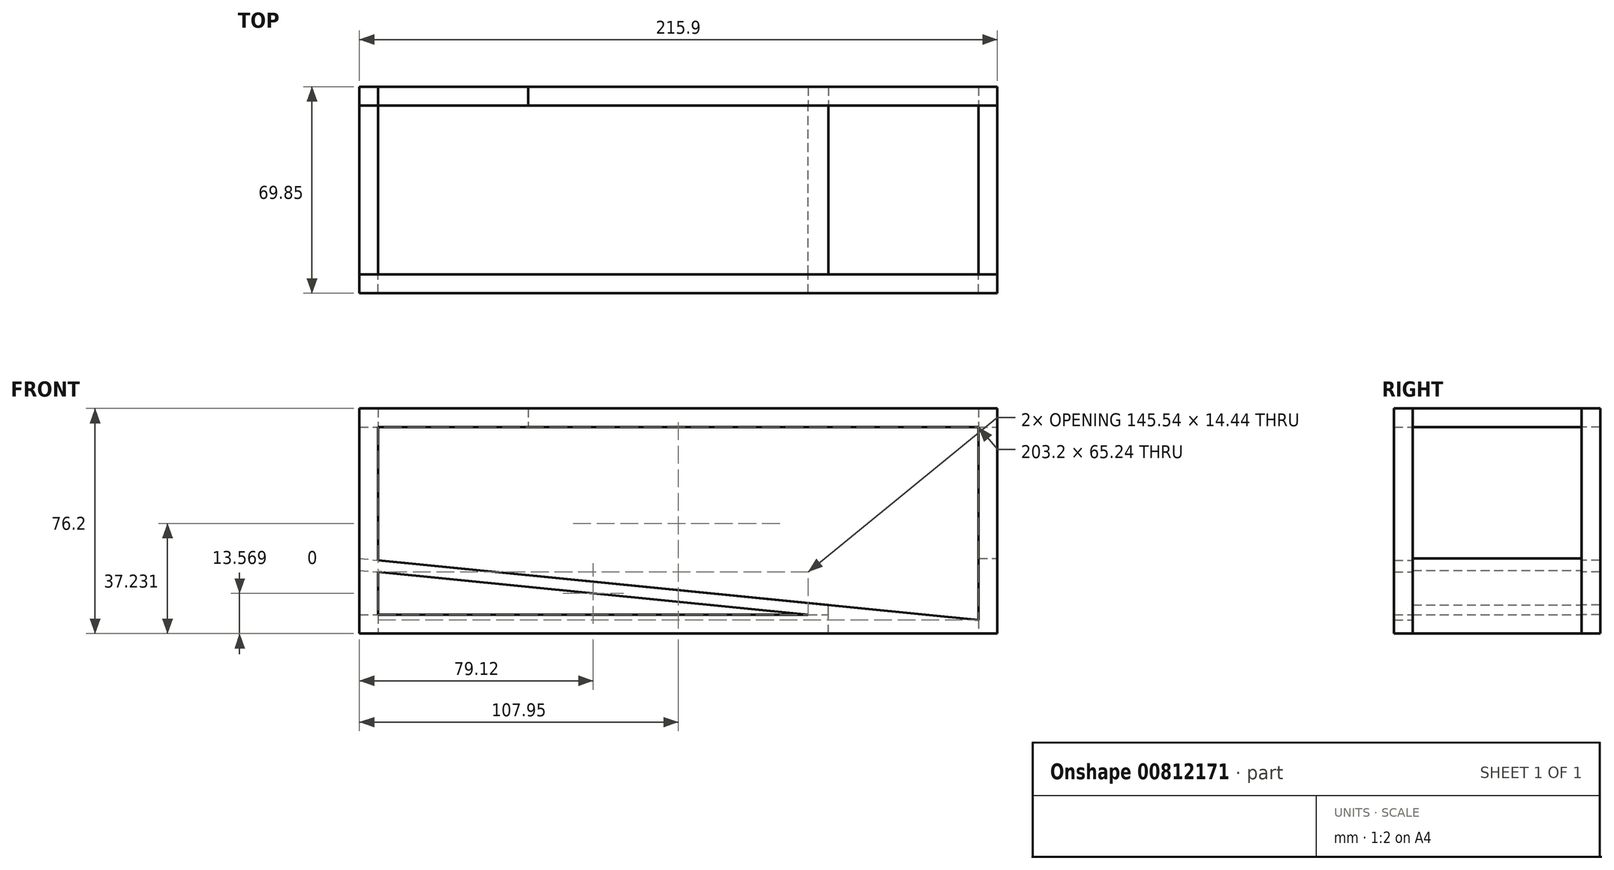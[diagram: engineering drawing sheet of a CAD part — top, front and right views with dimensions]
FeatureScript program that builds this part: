
annotation { "Feature Type Name" : "Feature", "Feature Type Description" : "" }
export const myFeature = defineFeature(function(context is Context, id is Id, definition is map)
    precondition{}
    {
        {
            var Q0;
            Q0=qCreatedBy(makeId("Front.planeOp"),FACE);
            var sketch = newSketch(context, id + "F0", { "sketchPlane" : qUnion([Q0])});
            skLineSegment(sketch, "E0.bottom", {"start": v(0, 76.2) * mm, "end": v(215.9, 76.2) * mm});
            skLineSegment(sketch, "E0.top", {"start": v(0, 0) * mm, "end": v(215.9, 0) * mm});
            skLineSegment(sketch, "E0.left", {"start": v(0, 76.2) * mm, "end": v(0, 0) * mm});
            skLineSegment(sketch, "E0.right", {"start": v(215.9, 76.2) * mm, "end": v(215.9, 0) * mm});
            skLineSegment(sketch, "E1.0", {"start": v(0, 69.85) * mm, "end": v(215.9, 69.85) * mm});
            skLineSegment(sketch, "E1.1", {"start": v(6.35, 76.2) * mm, "end": v(6.35, 0) * mm});
            skLineSegment(sketch, "E1.2", {"start": v(0, 6.35) * mm, "end": v(215.9, 6.35) * mm});
            skLineSegment(sketch, "E1.3", {"start": v(209.55, 76.2) * mm, "end": v(209.55, 0) * mm});
            skLineSegment(sketch, "E2", {"start": v(0, 25.4) * mm, "end": v(215.9, 3.98) * mm});
            skLineSegment(sketch, "E3.0", {"start": v(0, 21.42) * mm, "end": v(215.9, 0) * mm});
            skLineSegment(sketch, "E4", {"start": v(209.55, 25.4) * mm, "end": v(215.9, 25.4) * mm});
            skLineSegment(sketch, "E5.0", {"start": v(0, 29.38) * mm, "end": v(215.9, 7.96) * mm});
            skLineSegment(sketch, "E6", {"start": v(158.75, 0) * mm, "end": v(158.75, 13.63) * mm});
            skLineSegment(sketch, "E7", {"start": v(57.15, 76.2) * mm, "end": v(57.15, 69.85) * mm});
            skSolve(sketch);
        }
        {
            var Q0;
            {var subQ1=sQuery(id+"F0.wireOp",EDGE,"E1.1");var subQ5=sQuery(id+"F0.wireOp",EDGE,"E2");var subQ6=makeQuery(id+"F0.imprint","INTERSECT",VERTEX,{"derivedFrom":[subQ1,subQ5]});Q0=makeQuery(id+"F0.imprint","IMPRINT",FACE,{"disambiguationData":[TD([[makeQuery(id+"F0.imprint","IMPRINT",EDGE,{"disambiguationData":[TD([[subQ6,-1.0]])],"derivedFrom":subQ1}),1.0]])]});}
            var Q1;
            {var subQ0=sQuery(id+"F0.wireOp",EDGE,"E2");var subQ1=sQuery(id+"F0.wireOp",EDGE,"E0.left");var subQ2=makeQuery(id+"F0.imprint","INTERSECT",VERTEX,{"derivedFrom":[subQ1,subQ0]});Q1=makeQuery(id+"F0.imprint","IMPRINT",FACE,{"disambiguationData":[TD([[makeQuery(id+"F0.imprint","IMPRINT",EDGE,{"disambiguationData":[TD([[subQ2,-1.0]])],"derivedFrom":subQ1}),1.0]])]});}
            var Q2;
            {var subQ0=sQuery(id+"F0.wireOp",EDGE,"E2");var subQ1=sQuery(id+"F0.wireOp",EDGE,"E0.left");var subQ2=makeQuery(id+"F0.imprint","INTERSECT",VERTEX,{"derivedFrom":[subQ1,subQ0]});Q2=makeQuery(id+"F0.imprint","IMPRINT",FACE,{"disambiguationData":[TD([[makeQuery(id+"F0.imprint","IMPRINT",EDGE,{"disambiguationData":[TD([[subQ2,1.0]])],"derivedFrom":subQ1}),1.0]])]});}
            var Q3;
            {var subQ0=sQuery(id+"F0.wireOp",EDGE,"E1.0");var subQ1=sQuery(id+"F0.wireOp",EDGE,"E0.left");var subQ2=makeQuery(id+"F0.imprint","INTERSECT",VERTEX,{"derivedFrom":[subQ1,subQ0]});Q3=makeQuery(id+"F0.imprint","IMPRINT",FACE,{"disambiguationData":[TD([[makeQuery(id+"F0.imprint","IMPRINT",EDGE,{"disambiguationData":[TD([[subQ2,-1.0]])],"derivedFrom":subQ1}),1.0]])]});}
            var Q4;
            {var subQ0=sQuery(id+"F0.wireOp",EDGE,"E0.left");var subQ1=sQuery(id+"F0.wireOp",EDGE,"E0.bottom");var subQ2=makeQuery(id+"F0.imprint","INTERSECT",VERTEX,{"derivedFrom":[subQ1,subQ0]});Q4=makeQuery(id+"F0.imprint","IMPRINT",FACE,{"disambiguationData":[TD([[makeQuery(id+"F0.imprint","IMPRINT",EDGE,{"disambiguationData":[TD([[subQ2,-1.0]])],"derivedFrom":subQ1}),-1.0]])]});}
            var Q5;
            {var subQ0=sQuery(id+"F0.wireOp",EDGE,"E0.right");var subQ1=sQuery(id+"F0.wireOp",EDGE,"E0.bottom");var subQ2=makeQuery(id+"F0.imprint","INTERSECT",VERTEX,{"derivedFrom":[subQ1,subQ0]});Q5=makeQuery(id+"F0.imprint","IMPRINT",FACE,{"disambiguationData":[TD([[makeQuery(id+"F0.imprint","IMPRINT",EDGE,{"disambiguationData":[TD([[subQ2,1.0]])],"derivedFrom":subQ1}),-1.0]])]});}
            var Q6;
            {var subQ3=sQuery(id+"F0.wireOp",EDGE,"E4");Q6=makeQuery(id+"F0.imprint","IMPRINT",FACE,{"disambiguationData":[TD([[makeQuery(id+"F0.imprint","IMPRINT",EDGE,{"derivedFrom":subQ3}),1.0]])]});}
            var Q7;
            {var subQ0=sQuery(id+"F0.wireOp",EDGE,"E4");Q7=makeQuery(id+"F0.imprint","IMPRINT",FACE,{"disambiguationData":[TD([[makeQuery(id+"F0.imprint","IMPRINT",EDGE,{"derivedFrom":subQ0}),-1.0]])]});}
            var Q8;
            {var subQ0=sQuery(id+"F0.wireOp",EDGE,"E1.2");var subQ1=sQuery(id+"F0.wireOp",EDGE,"E0.right");var subQ2=makeQuery(id+"F0.imprint","INTERSECT",VERTEX,{"derivedFrom":[subQ1,subQ0]});Q8=makeQuery(id+"F0.imprint","IMPRINT",FACE,{"disambiguationData":[TD([[makeQuery(id+"F0.imprint","IMPRINT",EDGE,{"disambiguationData":[TD([[subQ2,1.0]])],"derivedFrom":subQ1}),-1.0]])]});}
            var Q9;
            {var subQ0=sQuery(id+"F0.wireOp",EDGE,"E1.2");var subQ1=sQuery(id+"F0.wireOp",EDGE,"E0.right");var subQ2=makeQuery(id+"F0.imprint","INTERSECT",VERTEX,{"derivedFrom":[subQ1,subQ0]});Q9=makeQuery(id+"F0.imprint","IMPRINT",FACE,{"disambiguationData":[TD([[makeQuery(id+"F0.imprint","IMPRINT",EDGE,{"disambiguationData":[TD([[subQ2,-1.0]])],"derivedFrom":subQ1}),-1.0]])]});}
            var Q10;
            {var subQ1=sQuery(id+"F0.wireOp",EDGE,"E0.top");var subQ3=sQuery(id+"F0.wireOp",EDGE,"E1.3");var subQ4=makeQuery(id+"F0.imprint","INTERSECT",VERTEX,{"derivedFrom":[subQ1,subQ3]});Q10=makeQuery(id+"F0.imprint","IMPRINT",FACE,{"disambiguationData":[TD([[makeQuery(id+"F0.imprint","IMPRINT",EDGE,{"disambiguationData":[TD([[subQ4,1.0]])],"derivedFrom":subQ3}),1.0]])]});}
            var Q11;
            {var subQ3=sQuery(id+"F0.wireOp",EDGE,"E2");var subQ5=sQuery(id+"F0.wireOp",EDGE,"E1.3");var subQ6=makeQuery(id+"F0.imprint","INTERSECT",VERTEX,{"derivedFrom":[subQ5,subQ3]});Q11=makeQuery(id+"F0.imprint","IMPRINT",FACE,{"disambiguationData":[TD([[makeQuery(id+"F0.imprint","IMPRINT",EDGE,{"disambiguationData":[TD([[subQ6,-1.0]])],"derivedFrom":subQ5}),1.0]])]});}
            var Q12;
            {var subQ0=sQuery(id+"F0.wireOp",EDGE,"E1.2");var subQ1=sQuery(id+"F0.wireOp",EDGE,"E0.left");var subQ2=makeQuery(id+"F0.imprint","INTERSECT",VERTEX,{"derivedFrom":[subQ1,subQ0]});Q12=makeQuery(id+"F0.imprint","IMPRINT",FACE,{"disambiguationData":[TD([[makeQuery(id+"F0.imprint","IMPRINT",EDGE,{"disambiguationData":[TD([[subQ2,1.0]])],"derivedFrom":subQ1}),1.0]])]});}
            var Q13;
            {var subQ0=sQuery(id+"F0.wireOp",EDGE,"E0.left");var subQ1=sQuery(id+"F0.wireOp",EDGE,"E0.top");var subQ2=makeQuery(id+"F0.imprint","INTERSECT",VERTEX,{"derivedFrom":[subQ1,subQ0]});Q13=makeQuery(id+"F0.imprint","IMPRINT",FACE,{"disambiguationData":[TD([[makeQuery(id+"F0.imprint","IMPRINT",EDGE,{"disambiguationData":[TD([[subQ2,-1.0]])],"derivedFrom":subQ1}),1.0]])]});}
            var Q14;
            {var subQ3=sQuery(id+"F0.wireOp",EDGE,"E7");Q14=makeQuery(id+"F0.imprint","IMPRINT",FACE,{"disambiguationData":[TD([[makeQuery(id+"F0.imprint","IMPRINT",EDGE,{"derivedFrom":subQ3}),1.0]])]});}
            var Q15;
            {var subQ0=sQuery(id+"F0.wireOp",EDGE,"E3.0");var subQ1=sQuery(id+"F0.wireOp",EDGE,"E1.2");var subQ2=makeQuery(id+"F0.imprint","INTERSECT",VERTEX,{"derivedFrom":[subQ1,subQ0]});Q15=makeQuery(id+"F0.imprint","IMPRINT",FACE,{"disambiguationData":[TD([[makeQuery(id+"F0.imprint","IMPRINT",EDGE,{"disambiguationData":[TD([[subQ2,-1.0]])],"derivedFrom":subQ1}),-1.0]])]});}
            var Q16;
            {var subQ1=sQuery(id+"F0.wireOp",EDGE,"E0.top");var subQ6=sQuery(id+"F0.wireOp",EDGE,"E1.1");var subQ9=makeQuery(id+"F0.imprint","INTERSECT",VERTEX,{"derivedFrom":[subQ1,subQ6]});Q16=makeQuery(id+"F0.imprint","IMPRINT",FACE,{"disambiguationData":[TD([[makeQuery(id+"F0.imprint","IMPRINT",EDGE,{"disambiguationData":[TD([[subQ9,-1.0]])],"derivedFrom":subQ1}),1.0]])]});}
            extrude(context, id + "F1", {"entities" : qUnion([Q0, Q1, Q2, Q3, Q4, Q5, Q6, Q7, Q8, Q9, Q10, Q11, Q12, Q13, Q14, Q15, Q16]), "oppositeDirection" : true, "depth" : 6.35 * mm, "offsetDistance" : 25.4 * mm});
        }
        {
            var Q0;
            {var subQ3=sQuery(id+"F0.wireOp",EDGE,"E2");var subQ5=sQuery(id+"F0.wireOp",EDGE,"E1.3");var subQ6=makeQuery(id+"F0.imprint","INTERSECT",VERTEX,{"derivedFrom":[subQ5,subQ3]});Q0=makeQuery(id+"F0.imprint","IMPRINT",FACE,{"disambiguationData":[TD([[makeQuery(id+"F0.imprint","IMPRINT",EDGE,{"disambiguationData":[TD([[subQ6,-1.0]])],"derivedFrom":subQ5}),1.0]])]});}
            var Q1;
            {var subQ1=sQuery(id+"F0.wireOp",EDGE,"E0.top");var subQ3=sQuery(id+"F0.wireOp",EDGE,"E1.3");var subQ4=makeQuery(id+"F0.imprint","INTERSECT",VERTEX,{"derivedFrom":[subQ1,subQ3]});Q1=makeQuery(id+"F0.imprint","IMPRINT",FACE,{"disambiguationData":[TD([[makeQuery(id+"F0.imprint","IMPRINT",EDGE,{"disambiguationData":[TD([[subQ4,1.0]])],"derivedFrom":subQ3}),1.0]])]});}
            var Q2;
            {var subQ0=sQuery(id+"F0.wireOp",EDGE,"E1.3");var subQ1=sQuery(id+"F0.wireOp",EDGE,"E0.top");var subQ2=makeQuery(id+"F0.imprint","INTERSECT",VERTEX,{"derivedFrom":[subQ1,subQ0]});Q2=makeQuery(id+"F0.imprint","IMPRINT",FACE,{"disambiguationData":[TD([[makeQuery(id+"F0.imprint","IMPRINT",EDGE,{"disambiguationData":[TD([[subQ2,1.0]])],"derivedFrom":subQ1}),1.0]])]});}
            var Q3;
            {var subQ3=sQuery(id+"F0.wireOp",EDGE,"E6");var subQ6=sQuery(id+"F0.wireOp",EDGE,"E1.2");var subQ9=makeQuery(id+"F0.imprint","INTERSECT",VERTEX,{"derivedFrom":[subQ6,subQ3]});Q3=makeQuery(id+"F0.imprint","IMPRINT",FACE,{"disambiguationData":[TD([[makeQuery(id+"F0.imprint","IMPRINT",EDGE,{"disambiguationData":[TD([[subQ9,-1.0]])],"derivedFrom":subQ6}),-1.0]])]});}
            var Q4;
            {var subQ0=sQuery(id+"F0.wireOp",EDGE,"E6");var subQ1=sQuery(id+"F0.wireOp",EDGE,"E1.2");var subQ2=makeQuery(id+"F0.imprint","INTERSECT",VERTEX,{"derivedFrom":[subQ1,subQ0]});Q4=makeQuery(id+"F0.imprint","IMPRINT",FACE,{"disambiguationData":[TD([[makeQuery(id+"F0.imprint","IMPRINT",EDGE,{"disambiguationData":[TD([[subQ2,-1.0]])],"derivedFrom":subQ1}),1.0]])]});}
            var Q5;
            {var subQ1=sQuery(id+"F0.wireOp",EDGE,"E1.1");var subQ5=sQuery(id+"F0.wireOp",EDGE,"E2");var subQ6=makeQuery(id+"F0.imprint","INTERSECT",VERTEX,{"derivedFrom":[subQ1,subQ5]});Q5=makeQuery(id+"F0.imprint","IMPRINT",FACE,{"disambiguationData":[TD([[makeQuery(id+"F0.imprint","IMPRINT",EDGE,{"disambiguationData":[TD([[subQ6,-1.0]])],"derivedFrom":subQ1}),1.0]])]});}
            var Q6;
            {var subQ0=sQuery(id+"F0.wireOp",EDGE,"E3.0");var subQ1=sQuery(id+"F0.wireOp",EDGE,"E1.2");var subQ2=makeQuery(id+"F0.imprint","INTERSECT",VERTEX,{"derivedFrom":[subQ1,subQ0]});Q6=makeQuery(id+"F0.imprint","IMPRINT",FACE,{"disambiguationData":[TD([[makeQuery(id+"F0.imprint","IMPRINT",EDGE,{"disambiguationData":[TD([[subQ2,-1.0]])],"derivedFrom":subQ1}),-1.0]])]});}
            var Q7;
            {var subQ1=sQuery(id+"F0.wireOp",EDGE,"E1.1");var subQ5=sQuery(id+"F0.wireOp",EDGE,"E0.top");var subQ6=makeQuery(id+"F0.imprint","INTERSECT",VERTEX,{"derivedFrom":[subQ5,subQ1]});Q7=makeQuery(id+"F0.imprint","IMPRINT",FACE,{"disambiguationData":[TD([[makeQuery(id+"F0.imprint","IMPRINT",EDGE,{"disambiguationData":[TD([[subQ6,-1.0]])],"derivedFrom":subQ5}),1.0]])]});}
            var Q8;
            {var subQ0=sQuery(id+"F0.wireOp",EDGE,"E4");Q8=makeQuery(id+"F0.imprint","IMPRINT",FACE,{"disambiguationData":[TD([[makeQuery(id+"F0.imprint","IMPRINT",EDGE,{"derivedFrom":subQ0}),-1.0]])]});}
            var Q9;
            {var subQ0=sQuery(id+"F0.wireOp",EDGE,"E1.2");var subQ1=sQuery(id+"F0.wireOp",EDGE,"E0.right");var subQ2=makeQuery(id+"F0.imprint","INTERSECT",VERTEX,{"derivedFrom":[subQ1,subQ0]});Q9=makeQuery(id+"F0.imprint","IMPRINT",FACE,{"disambiguationData":[TD([[makeQuery(id+"F0.imprint","IMPRINT",EDGE,{"disambiguationData":[TD([[subQ2,-1.0]])],"derivedFrom":subQ1}),-1.0]])]});}
            var Q10;
            {var subQ0=sQuery(id+"F0.wireOp",EDGE,"E1.2");var subQ1=sQuery(id+"F0.wireOp",EDGE,"E0.right");var subQ2=makeQuery(id+"F0.imprint","INTERSECT",VERTEX,{"derivedFrom":[subQ1,subQ0]});Q10=makeQuery(id+"F0.imprint","IMPRINT",FACE,{"disambiguationData":[TD([[makeQuery(id+"F0.imprint","IMPRINT",EDGE,{"disambiguationData":[TD([[subQ2,1.0]])],"derivedFrom":subQ1}),-1.0]])]});}
            var Q11;
            {var subQ3=sQuery(id+"F0.wireOp",EDGE,"E4");Q11=makeQuery(id+"F0.imprint","IMPRINT",FACE,{"disambiguationData":[TD([[makeQuery(id+"F0.imprint","IMPRINT",EDGE,{"derivedFrom":subQ3}),1.0]])]});}
            var Q12;
            {var subQ0=sQuery(id+"F0.wireOp",EDGE,"E0.right");var subQ1=sQuery(id+"F0.wireOp",EDGE,"E0.bottom");var subQ2=makeQuery(id+"F0.imprint","INTERSECT",VERTEX,{"derivedFrom":[subQ1,subQ0]});Q12=makeQuery(id+"F0.imprint","IMPRINT",FACE,{"disambiguationData":[TD([[makeQuery(id+"F0.imprint","IMPRINT",EDGE,{"disambiguationData":[TD([[subQ2,1.0]])],"derivedFrom":subQ1}),-1.0]])]});}
            var Q13;
            {var subQ3=sQuery(id+"F0.wireOp",EDGE,"E7");Q13=makeQuery(id+"F0.imprint","IMPRINT",FACE,{"disambiguationData":[TD([[makeQuery(id+"F0.imprint","IMPRINT",EDGE,{"derivedFrom":subQ3}),1.0]])]});}
            var Q14;
            {var subQ0=sQuery(id+"F0.wireOp",EDGE,"E0.left");var subQ1=sQuery(id+"F0.wireOp",EDGE,"E0.top");var subQ2=makeQuery(id+"F0.imprint","INTERSECT",VERTEX,{"derivedFrom":[subQ1,subQ0]});Q14=makeQuery(id+"F0.imprint","IMPRINT",FACE,{"disambiguationData":[TD([[makeQuery(id+"F0.imprint","IMPRINT",EDGE,{"disambiguationData":[TD([[subQ2,-1.0]])],"derivedFrom":subQ1}),1.0]])]});}
            var Q15;
            {var subQ0=sQuery(id+"F0.wireOp",EDGE,"E1.2");var subQ1=sQuery(id+"F0.wireOp",EDGE,"E0.left");var subQ2=makeQuery(id+"F0.imprint","INTERSECT",VERTEX,{"derivedFrom":[subQ1,subQ0]});Q15=makeQuery(id+"F0.imprint","IMPRINT",FACE,{"disambiguationData":[TD([[makeQuery(id+"F0.imprint","IMPRINT",EDGE,{"disambiguationData":[TD([[subQ2,1.0]])],"derivedFrom":subQ1}),1.0]])]});}
            var Q16;
            {var subQ0=sQuery(id+"F0.wireOp",EDGE,"E2");var subQ1=sQuery(id+"F0.wireOp",EDGE,"E0.left");var subQ2=makeQuery(id+"F0.imprint","INTERSECT",VERTEX,{"derivedFrom":[subQ1,subQ0]});Q16=makeQuery(id+"F0.imprint","IMPRINT",FACE,{"disambiguationData":[TD([[makeQuery(id+"F0.imprint","IMPRINT",EDGE,{"disambiguationData":[TD([[subQ2,-1.0]])],"derivedFrom":subQ1}),1.0]])]});}
            var Q17;
            {var subQ0=sQuery(id+"F0.wireOp",EDGE,"E2");var subQ1=sQuery(id+"F0.wireOp",EDGE,"E0.left");var subQ2=makeQuery(id+"F0.imprint","INTERSECT",VERTEX,{"derivedFrom":[subQ1,subQ0]});Q17=makeQuery(id+"F0.imprint","IMPRINT",FACE,{"disambiguationData":[TD([[makeQuery(id+"F0.imprint","IMPRINT",EDGE,{"disambiguationData":[TD([[subQ2,1.0]])],"derivedFrom":subQ1}),1.0]])]});}
            var Q18;
            {var subQ0=sQuery(id+"F0.wireOp",EDGE,"E1.0");var subQ1=sQuery(id+"F0.wireOp",EDGE,"E0.left");var subQ2=makeQuery(id+"F0.imprint","INTERSECT",VERTEX,{"derivedFrom":[subQ1,subQ0]});Q18=makeQuery(id+"F0.imprint","IMPRINT",FACE,{"disambiguationData":[TD([[makeQuery(id+"F0.imprint","IMPRINT",EDGE,{"disambiguationData":[TD([[subQ2,-1.0]])],"derivedFrom":subQ1}),1.0]])]});}
            var Q19;
            {var subQ0=sQuery(id+"F0.wireOp",EDGE,"E0.left");var subQ1=sQuery(id+"F0.wireOp",EDGE,"E0.bottom");var subQ2=makeQuery(id+"F0.imprint","INTERSECT",VERTEX,{"derivedFrom":[subQ1,subQ0]});Q19=makeQuery(id+"F0.imprint","IMPRINT",FACE,{"disambiguationData":[TD([[makeQuery(id+"F0.imprint","IMPRINT",EDGE,{"disambiguationData":[TD([[subQ2,-1.0]])],"derivedFrom":subQ1}),-1.0]])]});}
            var Q20;
            {var subQ3=sQuery(id+"F0.wireOp",EDGE,"E7");Q20=makeQuery(id+"F0.imprint","IMPRINT",FACE,{"disambiguationData":[TD([[makeQuery(id+"F0.imprint","IMPRINT",EDGE,{"derivedFrom":subQ3}),-1.0]])]});}
            extrude(context, id + "F2", {"entities" : qUnion([Q0, Q1, Q2, Q3, Q4, Q5, Q6, Q7, Q8, Q9, Q10, Q11, Q12, Q13, Q14, Q15, Q16, Q17, Q18, Q19, Q20]), "depth" : 63.5 * mm, "offsetDistance" : 25.4 * mm, "hasSecondDirection" : true, "secondDirectionOppositeDirection" : true, "secondDirectionDepth" : -57.15 * mm});
        }
        {
            var Q0;
            {var subQ0=sQuery(id+"F0.wireOp",EDGE,"E0.right");var subQ1=sQuery(id+"F0.wireOp",EDGE,"E0.bottom");var subQ2=makeQuery(id+"F0.imprint","INTERSECT",VERTEX,{"derivedFrom":[subQ1,subQ0]});Q0=makeQuery(id+"F0.imprint","IMPRINT",FACE,{"disambiguationData":[TD([[makeQuery(id+"F0.imprint","IMPRINT",EDGE,{"disambiguationData":[TD([[subQ2,1.0]])],"derivedFrom":subQ1}),-1.0]])]});}
            var Q1;
            {var subQ1=sQuery(id+"F0.wireOp",EDGE,"E0.top");var subQ3=sQuery(id+"F0.wireOp",EDGE,"E1.3");var subQ4=makeQuery(id+"F0.imprint","INTERSECT",VERTEX,{"derivedFrom":[subQ1,subQ3]});Q1=makeQuery(id+"F0.imprint","IMPRINT",FACE,{"disambiguationData":[TD([[makeQuery(id+"F0.imprint","IMPRINT",EDGE,{"disambiguationData":[TD([[subQ4,1.0]])],"derivedFrom":subQ3}),1.0]])]});}
            var Q2;
            {var subQ3=sQuery(id+"F0.wireOp",EDGE,"E2");var subQ5=sQuery(id+"F0.wireOp",EDGE,"E1.3");var subQ6=makeQuery(id+"F0.imprint","INTERSECT",VERTEX,{"derivedFrom":[subQ5,subQ3]});Q2=makeQuery(id+"F0.imprint","IMPRINT",FACE,{"disambiguationData":[TD([[makeQuery(id+"F0.imprint","IMPRINT",EDGE,{"disambiguationData":[TD([[subQ6,-1.0]])],"derivedFrom":subQ5}),1.0]])]});}
            var Q3;
            {var subQ0=sQuery(id+"F0.wireOp",EDGE,"E1.2");var subQ1=sQuery(id+"F0.wireOp",EDGE,"E0.right");var subQ2=makeQuery(id+"F0.imprint","INTERSECT",VERTEX,{"derivedFrom":[subQ1,subQ0]});Q3=makeQuery(id+"F0.imprint","IMPRINT",FACE,{"disambiguationData":[TD([[makeQuery(id+"F0.imprint","IMPRINT",EDGE,{"disambiguationData":[TD([[subQ2,-1.0]])],"derivedFrom":subQ1}),-1.0]])]});}
            var Q4;
            {var subQ0=sQuery(id+"F0.wireOp",EDGE,"E1.2");var subQ1=sQuery(id+"F0.wireOp",EDGE,"E0.right");var subQ2=makeQuery(id+"F0.imprint","INTERSECT",VERTEX,{"derivedFrom":[subQ1,subQ0]});Q4=makeQuery(id+"F0.imprint","IMPRINT",FACE,{"disambiguationData":[TD([[makeQuery(id+"F0.imprint","IMPRINT",EDGE,{"disambiguationData":[TD([[subQ2,1.0]])],"derivedFrom":subQ1}),-1.0]])]});}
            var Q5;
            {var subQ0=sQuery(id+"F0.wireOp",EDGE,"E4");Q5=makeQuery(id+"F0.imprint","IMPRINT",FACE,{"disambiguationData":[TD([[makeQuery(id+"F0.imprint","IMPRINT",EDGE,{"derivedFrom":subQ0}),-1.0]])]});}
            var Q6;
            {var subQ0=sQuery(id+"F0.wireOp",EDGE,"E0.left");var subQ1=sQuery(id+"F0.wireOp",EDGE,"E0.bottom");var subQ2=makeQuery(id+"F0.imprint","INTERSECT",VERTEX,{"derivedFrom":[subQ1,subQ0]});Q6=makeQuery(id+"F0.imprint","IMPRINT",FACE,{"disambiguationData":[TD([[makeQuery(id+"F0.imprint","IMPRINT",EDGE,{"disambiguationData":[TD([[subQ2,-1.0]])],"derivedFrom":subQ1}),-1.0]])]});}
            var Q7;
            {var subQ0=sQuery(id+"F0.wireOp",EDGE,"E0.left");var subQ1=sQuery(id+"F0.wireOp",EDGE,"E0.top");var subQ2=makeQuery(id+"F0.imprint","INTERSECT",VERTEX,{"derivedFrom":[subQ1,subQ0]});Q7=makeQuery(id+"F0.imprint","IMPRINT",FACE,{"disambiguationData":[TD([[makeQuery(id+"F0.imprint","IMPRINT",EDGE,{"disambiguationData":[TD([[subQ2,-1.0]])],"derivedFrom":subQ1}),1.0]])]});}
            var Q8;
            {var subQ0=sQuery(id+"F0.wireOp",EDGE,"E2");var subQ1=sQuery(id+"F0.wireOp",EDGE,"E0.left");var subQ2=makeQuery(id+"F0.imprint","INTERSECT",VERTEX,{"derivedFrom":[subQ1,subQ0]});Q8=makeQuery(id+"F0.imprint","IMPRINT",FACE,{"disambiguationData":[TD([[makeQuery(id+"F0.imprint","IMPRINT",EDGE,{"disambiguationData":[TD([[subQ2,-1.0]])],"derivedFrom":subQ1}),1.0]])]});}
            var Q9;
            {var subQ1=sQuery(id+"F0.wireOp",EDGE,"E1.1");var subQ5=sQuery(id+"F0.wireOp",EDGE,"E2");var subQ6=makeQuery(id+"F0.imprint","INTERSECT",VERTEX,{"derivedFrom":[subQ1,subQ5]});Q9=makeQuery(id+"F0.imprint","IMPRINT",FACE,{"disambiguationData":[TD([[makeQuery(id+"F0.imprint","IMPRINT",EDGE,{"disambiguationData":[TD([[subQ6,-1.0]])],"derivedFrom":subQ1}),1.0]])]});}
            extrude(context, id + "F3", {"entities" : qUnion([Q0, Q1, Q2, Q3, Q4, Q5, Q6, Q7, Q8, Q9]), "depth" : 57.15 * mm, "offsetDistance" : 25.4 * mm});
        }
    });
